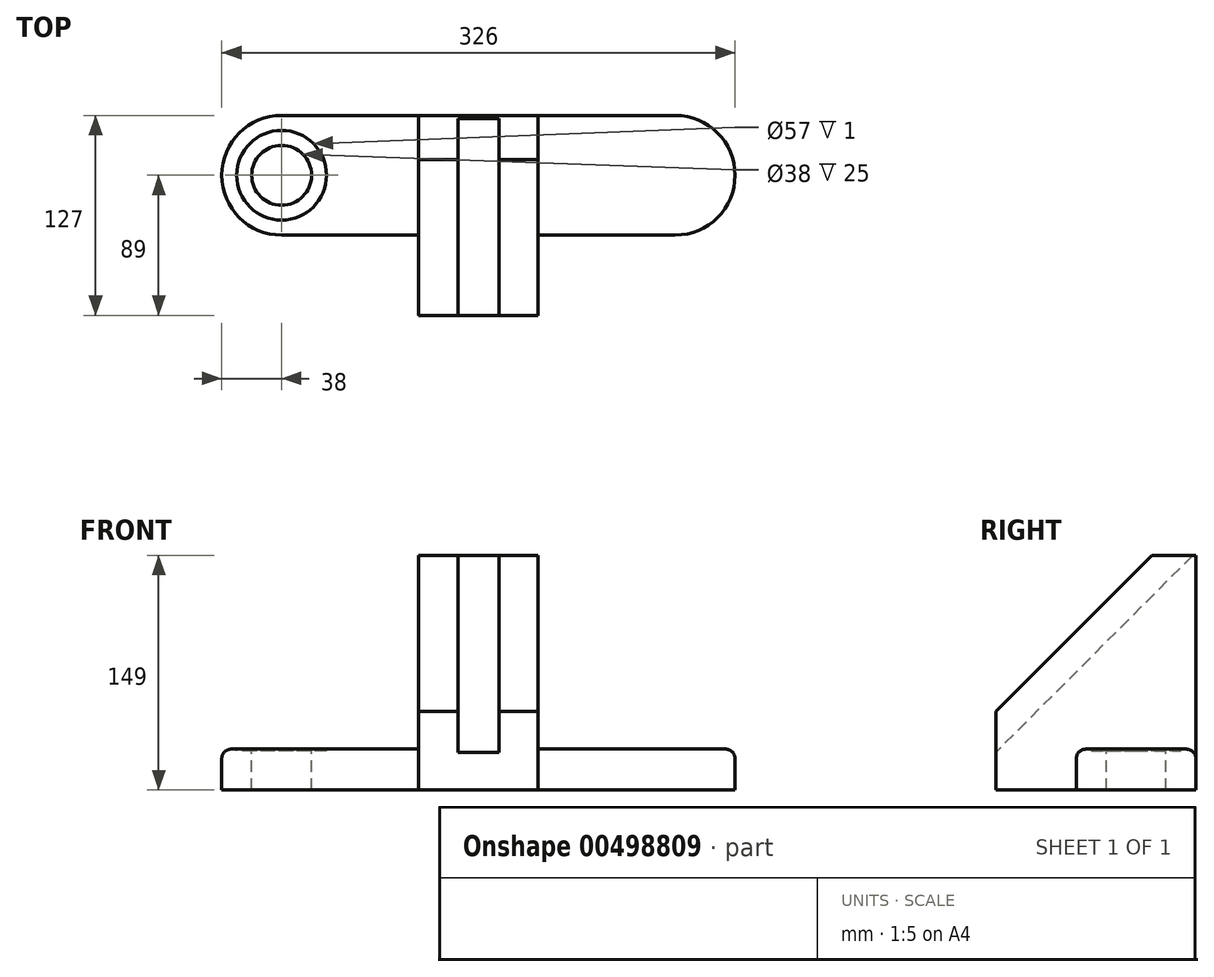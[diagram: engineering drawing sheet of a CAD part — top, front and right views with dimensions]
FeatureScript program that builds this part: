
annotation { "Feature Type Name" : "Feature", "Feature Type Description" : "" }
export const myFeature = defineFeature(function(context is Context, id is Id, definition is map)
    precondition{}
    {
        {
            var Q0;
            Q0=qCreatedBy(makeId("Right.planeOp"),FACE);
            var sketch = newSketch(context, id + "F0", { "sketchPlane" : qUnion([Q0])});
            skLineSegment(sketch, "E0", {"start": v(0, 0) * mm, "end": v(0, 149) * mm});
            skLineSegment(sketch, "E1", {"start": v(0, 149) * mm, "end": v(-28, 149) * mm});
            skLineSegment(sketch, "E2", {"start": v(-28, 149) * mm, "end": v(-127, 50) * mm});
            skLineSegment(sketch, "E3", {"start": v(-127, 50) * mm, "end": v(-127, 0) * mm});
            skLineSegment(sketch, "E4", {"start": v(-127, 0) * mm, "end": v(0, 0) * mm});
            skSolve(sketch);
        }
        {
            var Q0;
            Q0=qSketchRegion(id+"F0",true);
            extrude(context, id + "F1", {"entities" : qUnion([Q0]), "endBound" : BoundingType.SYMMETRIC, "depth" : 76 * mm});
        }
        {
            var Q0;
            Q0=qCreatedBy(makeId("Right.planeOp"),FACE);
            var sketch = newSketch(context, id + "F2", { "sketchPlane" : qUnion([Q0])});
            skLineSegment(sketch, "E5", {"start": v(-2, 149) * mm, "end": v(-127, 24) * mm});
            skLineSegment(sketch, "E6", {"start": v(-127, 24) * mm, "end": v(-127, 50) * mm});
            skLineSegment(sketch, "E7", {"start": v(-127, 50) * mm, "end": v(-28, 149) * mm});
            skLineSegment(sketch, "E8", {"start": v(-28, 149) * mm, "end": v(-2, 149) * mm});
            skSolve(sketch);
        }
        {
            var Q0;
            Q0=qSketchRegion(id+"F2",true);
            extrude(context, id + "F3", {"entities" : qUnion([Q0]), "operationType" : NewBodyOperationType.REMOVE, "endBound" : BoundingType.SYMMETRIC, "oppositeDirection" : true, "depth" : 26 * mm});
        }
        {
            var Q0;
            Q0=qCreatedBy(makeId("Top.planeOp"),FACE);
            var sketch = newSketch(context, id + "F4", { "sketchPlane" : qUnion([Q0])});
            skLineSegment(sketch, "E9", {"start": v(-125, -38) * mm, "end": v(125, -38) * mm, "construction": true});
            skPoint(sketch, "E10", {"position": v(0, -38) * mm});
            skArc(sketch, "E11.0.startCap", {"start": v(-125, -76) * mm, "mid": v(-163, -38) * mm, "end": v(-125, 0) * mm});
            skArc(sketch, "E11.0.endCap", {"start": v(125, 0) * mm, "mid": v(163, -38) * mm, "end": v(125, -76) * mm});
            skLineSegment(sketch, "E11.0.left", {"start": v(-125, 0) * mm, "end": v(125, 0) * mm});
            skLineSegment(sketch, "E11.0.right", {"start": v(-125, -76) * mm, "end": v(125, -76) * mm});
            skSolve(sketch);
        }
        {
            var Q0;
            Q0=qSketchRegion(id+"F4",true);
            extrude(context, id + "F5", {"entities" : qUnion([Q0]), "operationType" : NewBodyOperationType.ADD, "depth" : 26 * mm});
        }
        {
            var Q0;
            {var subQ0=sQuery(id+"F4.wireOp",EDGE,"E11.0.startCap");var subQ1=sQuery(id+"F4.wireOp",EDGE,"E11.0.left");var subQ3=sQuery(id+"F4.wireOp",EDGE,"E11.0.right");Q0=makeQuery(id+"F5.boolean.opBoolean","SPLIT",FACE,{"disambiguationData":[TD([makeQuery(id+"F5.opExtrude","SWEPT_FACE",FACE,{"disambiguationData":[OSD([subQ0])]})])],"derivedFrom":makeQuery(id+"F5.opExtrude","CAP_FACE",FACE,{"disambiguationData":[OSD([subQ0,sQuery(id+"F4.wireOp",EDGE,"E11.0.endCap"),subQ1,subQ3])],"isStart":false})});}
            var sketch = newSketch(context, id + "F6", { "sketchPlane" : qUnion([Q0])});
            skCircle(sketch, "E12", {"center": v(-125, -38) * mm, "radius": 28.5 * mm});
            skSolve(sketch);
        }
        {
            var Q0;
            Q0=qSketchRegion(id+"F6",true);
            extrude(context, id + "F7", {"entities" : qUnion([Q0]), "operationType" : NewBodyOperationType.REMOVE, "oppositeDirection" : true, "depth" : 1 * mm});
        }
        {
            var Q0;
            Q0=makeQuery(id+"F7.boolean.opBoolean","COPY",FACE,{"derivedFrom":makeQuery(id+"F7.opExtrude","CAP_FACE",FACE,{"disambiguationData":[OSD([sQuery(id+"F6.wireOp",EDGE,"E12")])],"isStart":false})});
            var sketch = newSketch(context, id + "F8", { "sketchPlane" : qUnion([Q0])});
            skCircle(sketch, "E13", {"center": v(-125, -38) * mm, "radius": 19 * mm});
            skSolve(sketch);
        }
        {
            var Q0;
            Q0=qSketchRegion(id+"F8",true);
            extrude(context, id + "F9", {"entities" : qUnion([Q0]), "operationType" : NewBodyOperationType.REMOVE, "endBound" : BoundingType.UP_TO_NEXT, "oppositeDirection" : true, "depth" : 25 * mm});
        }
        {
            var Q0;
            {var subQ0=sQuery(id+"F4.wireOp",EDGE,"E11.0.startCap");var subQ1=sQuery(id+"F4.wireOp",EDGE,"E11.0.right");Q0=makeQuery(id+"F5.boolean.opBoolean","SPLIT",EDGE,{"disambiguationData":[TD([makeQuery(id+"F5.opExtrude","SWEPT_FACE",FACE,{"disambiguationData":[OSD([subQ0])]})])],"derivedFrom":makeQuery(id+"F5.opExtrude","CAP_EDGE",EDGE,{"disambiguationData":[OSD([subQ1])],"isStart":false})});}
            var Q1;
            {var subQ0=sQuery(id+"F4.wireOp",EDGE,"E11.0.left");var subQ1=sQuery(id+"F4.wireOp",EDGE,"E11.0.endCap");Q1=makeQuery(id+"F5.boolean.opBoolean","SPLIT",EDGE,{"disambiguationData":[TD([makeQuery(id+"F5.opExtrude","SWEPT_FACE",FACE,{"disambiguationData":[OSD([subQ1])]})])],"derivedFrom":makeQuery(id+"F5.opExtrude","CAP_EDGE",EDGE,{"disambiguationData":[OSD([subQ0])],"isStart":false})});}
            fillet(context, id + "F10", {"entities" : qUnion([Q0, Q1]), "radius" : 6 * mm, "tangentPropagation" : true, "allowEdgeOverflow" : false});
        }
    });
